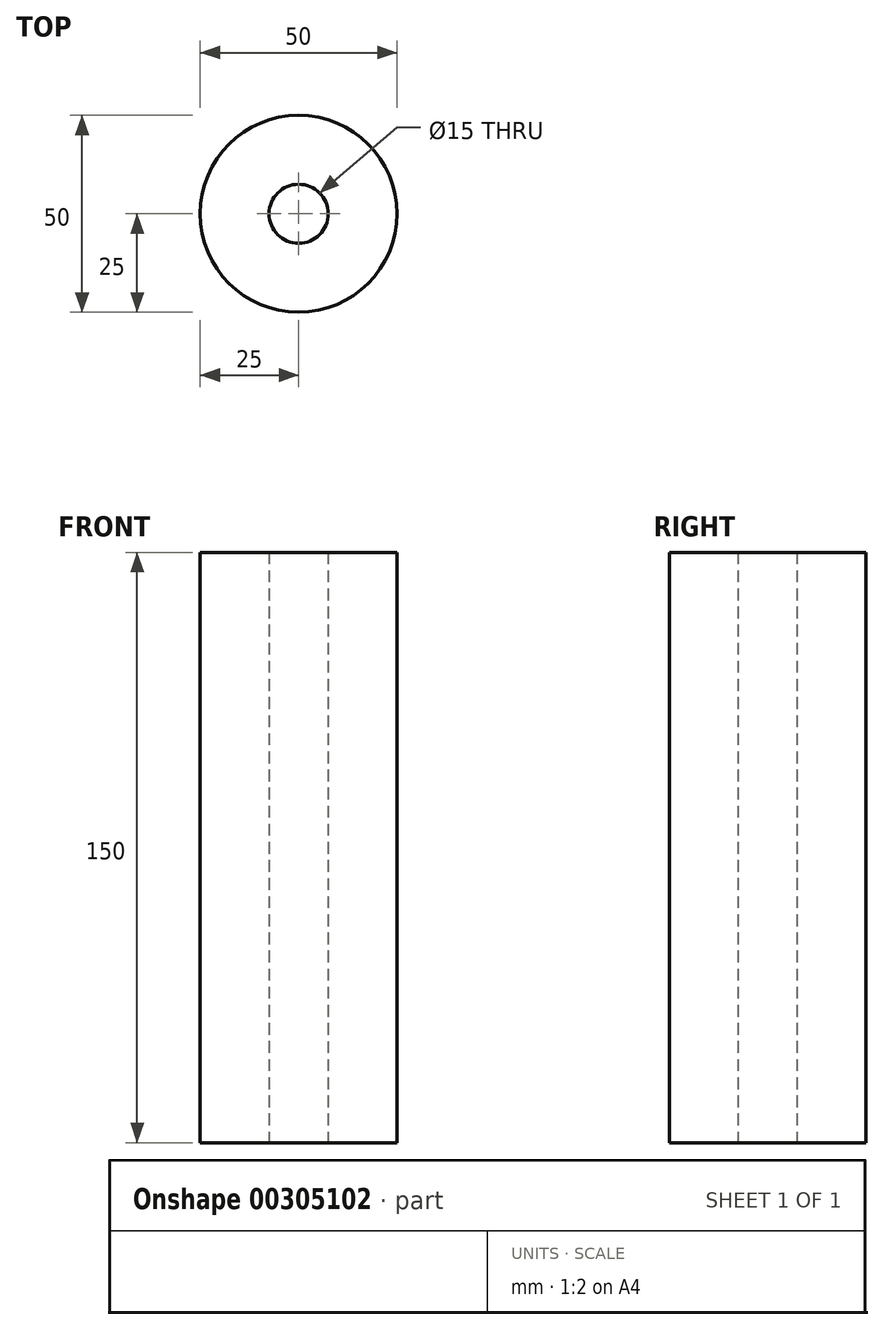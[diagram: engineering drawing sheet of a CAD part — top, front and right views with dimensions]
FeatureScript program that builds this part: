
annotation { "Feature Type Name" : "Feature", "Feature Type Description" : "" }
export const myFeature = defineFeature(function(context is Context, id is Id, definition is map)
    precondition{}
    {
        {
            var Q0;
            Q0=qCreatedBy(makeId("Top.planeOp"),FACE);
            var sketch = newSketch(context, id + "F0", { "sketchPlane" : qUnion([Q0])});
            skCircle(sketch, "E0", {"center": v(0, 0) * mm, "radius": 25 * mm});
            skCircle(sketch, "E1", {"center": v(0, 0) * mm, "radius": 7.5 * mm});
            skSolve(sketch);
        }
        {
            var Q0;
            Q0 = qSketchRegion(id + "F0", true);
            extrude(context, id + "F1", {"entities" : qUnion([Q0]), "depth" : 150 * mm, "symmetric" : true});
        }
    });
